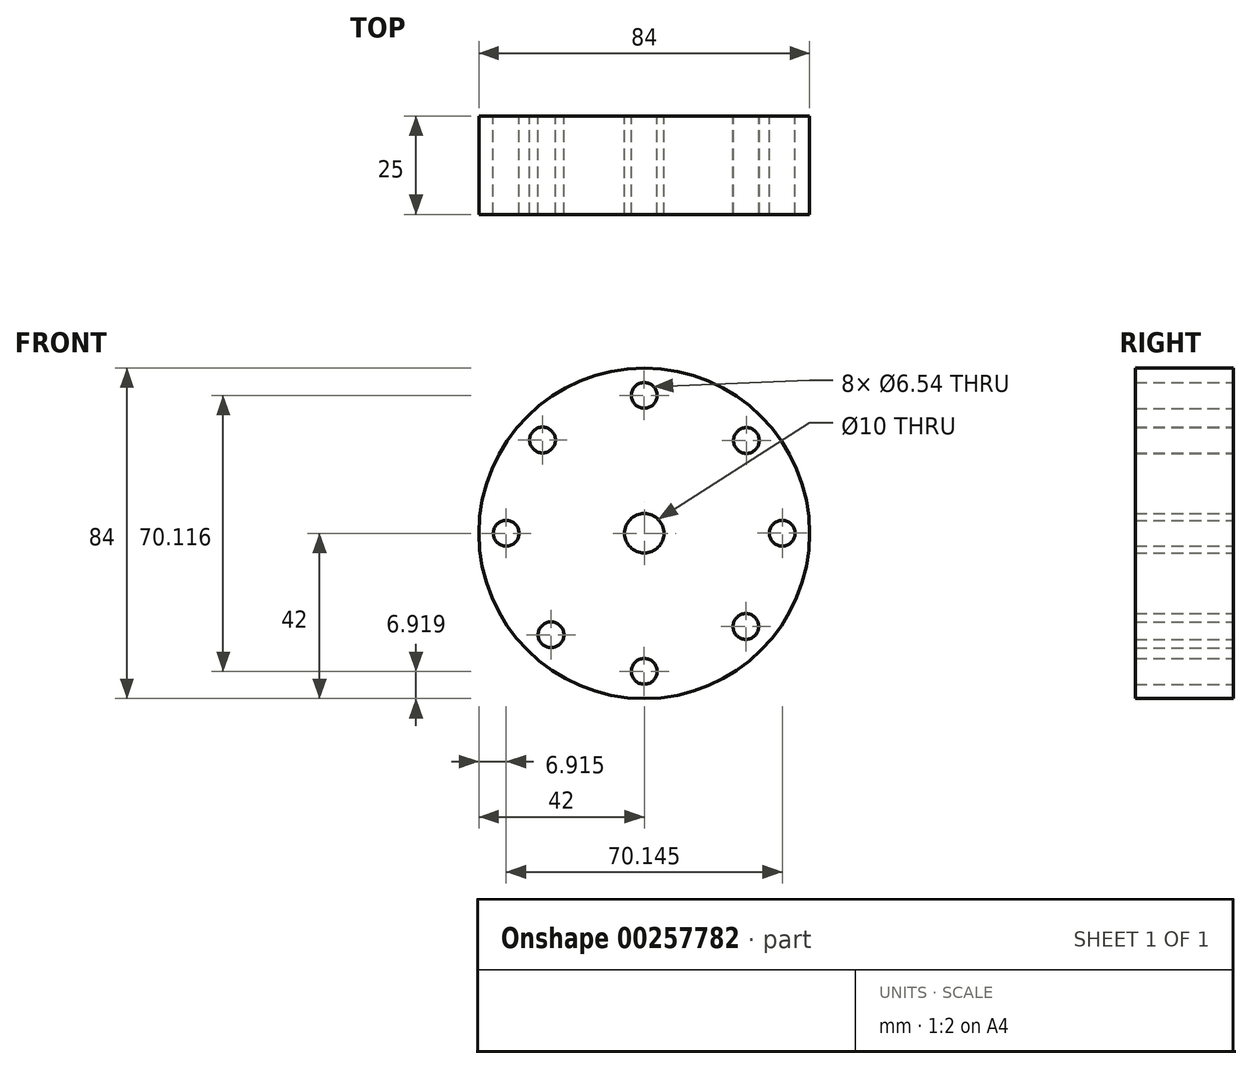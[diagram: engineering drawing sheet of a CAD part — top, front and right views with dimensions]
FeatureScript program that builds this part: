
annotation { "Feature Type Name" : "Feature", "Feature Type Description" : "" }
export const myFeature = defineFeature(function(context is Context, id is Id, definition is map)
    precondition{}
    {
        {
            var Q0;
            Q0=qCreatedBy(makeId("Front.planeOp"),FACE);
            var sketch = newSketch(context, id + "F0", { "sketchPlane" : qUnion([Q0])});
            skCircle(sketch, "E0", {"center": v(0, 0) * mm, "radius": 42 * mm});
            skCircle(sketch, "E1", {"center": v(0, 0) * mm, "radius": 15 * mm});
            skCircle(sketch, "E2", {"center": v(0, 0) * mm, "radius": 8.75 * mm});
            skCircle(sketch, "E3", {"center": v(-25.85, 23.71) * mm, "radius": 3.27 * mm});
            skCircle(sketch, "E4", {"center": v(0, 35.04) * mm, "radius": 3.27 * mm});
            skCircle(sketch, "E5", {"center": v(25.96, 23.59) * mm, "radius": 3.27 * mm});
            skCircle(sketch, "E6", {"center": v(35.06, 0.02) * mm, "radius": 3.27 * mm});
            skCircle(sketch, "E7", {"center": v(25.82, -23.68) * mm, "radius": 3.27 * mm});
            skCircle(sketch, "E8", {"center": v(-0.01, -35.08) * mm, "radius": 3.27 * mm});
            skCircle(sketch, "E9", {"center": v(-23.7, -25.8) * mm, "radius": 3.27 * mm});
            skCircle(sketch, "E10", {"center": v(-35.09, 0.02) * mm, "radius": 3.27 * mm});
            skCircle(sketch, "E11", {"center": v(0, 0) * mm, "radius": 5 * mm});
            skSolve(sketch);
        }
        {
            var Q0;
            Q0=makeQuery(id+"F0.imprint","IMPRINT",FACE,{"disambiguationData":[TD([[makeQuery(id+"F0.imprint","IMPRINT",EDGE,{"derivedFrom":sQuery(id+"F0.wireOp",EDGE,"E0")}),1.0]])]});
            var Q1;
            Q1=makeQuery(id+"F0.imprint","IMPRINT",FACE,{"disambiguationData":[TD([[makeQuery(id+"F0.imprint","IMPRINT",EDGE,{"derivedFrom":sQuery(id+"F0.wireOp",EDGE,"E1")}),1.0]])]});
            extrude(context, id + "F1", {"entities" : qUnion([Q0, Q1]), "depth" : 25 * mm});
        }
        {
            var Q0;
            Q0=makeQuery(id+"F0.imprint","IMPRINT",FACE,{"disambiguationData":[TD([[makeQuery(id+"F0.imprint","IMPRINT",EDGE,{"derivedFrom":sQuery(id+"F0.wireOp",EDGE,"E2")}),1.0]])]});
            extrude(context, id + "F2", {"entities" : qUnion([Q0]), "operationType" : NewBodyOperationType.ADD, "depth" : 25 * mm});
        }
        {
            var Q0;
            Q0=sQuery(id+"F0.wireOp",EDGE,"E11");
            var Q1;
            Q1=sQuery(id+"F0.wireOp",EDGE,"E2");
            extrude(context, id + "F3", {"bodyType" : ToolBodyType.SURFACE, "surfaceEntities" : qUnion([Q0, Q1]), "depth" : 25 * mm});
        }
        {
            var Q0;
            Q0=sQuery(id+"F0.wireOp",EDGE,"E11");
            extrude(context, id + "F4", {"bodyType" : ToolBodyType.SURFACE, "surfaceEntities" : qUnion([Q0]), "depth" : 25 * mm});
        }
        {
            var Q0;
            Q0=sQuery(id+"F0.wireOp",EDGE,"E11");
            var Q1;
            Q1=sQuery(id+"F0.wireOp",EDGE,"E1");
            extrude(context, id + "F5", {"bodyType" : ToolBodyType.SURFACE, "surfaceEntities" : qUnion([Q0, Q1]), "depth" : 25 * mm});
        }
        {
            var Q0;
            Q0=sQuery(id+"F0.wireOp",EDGE,"E11");
            extrude(context, id + "F6", {"bodyType" : ToolBodyType.SURFACE, "surfaceEntities" : qUnion([Q0]), "depth" : 21 * mm});
        }
        {
            var Q0;
            {var subQ0=sQuery(id+"F0.wireOp",EDGE,"E2");Q0=makeQuery(id+"F2.boolean.opBoolean","MERGE",FACE,{"derivedFrom":[makeQuery(id+"F1.opExtrude","CAP_FACE",FACE,{"disambiguationData":[OSD([sQuery(id+"F0.wireOp",EDGE,"E0"),subQ0,sQuery(id+"F0.wireOp",EDGE,"E3"),sQuery(id+"F0.wireOp",EDGE,"E4"),sQuery(id+"F0.wireOp",EDGE,"E5"),sQuery(id+"F0.wireOp",EDGE,"E6"),sQuery(id+"F0.wireOp",EDGE,"E7"),sQuery(id+"F0.wireOp",EDGE,"E8"),sQuery(id+"F0.wireOp",EDGE,"E9"),sQuery(id+"F0.wireOp",EDGE,"E10")])],"isStart":false}),makeQuery(id+"F2.opExtrude","CAP_FACE",FACE,{"disambiguationData":[OSD([subQ0,sQuery(id+"F0.wireOp",EDGE,"E11")])],"isStart":false})]});}
            extrude(context, id + "F7", {"entities" : qUnion([Q0]), "operationType" : NewBodyOperationType.ADD, "oppositeDirection" : true, "depth" : 24 * mm});
        }
    });
